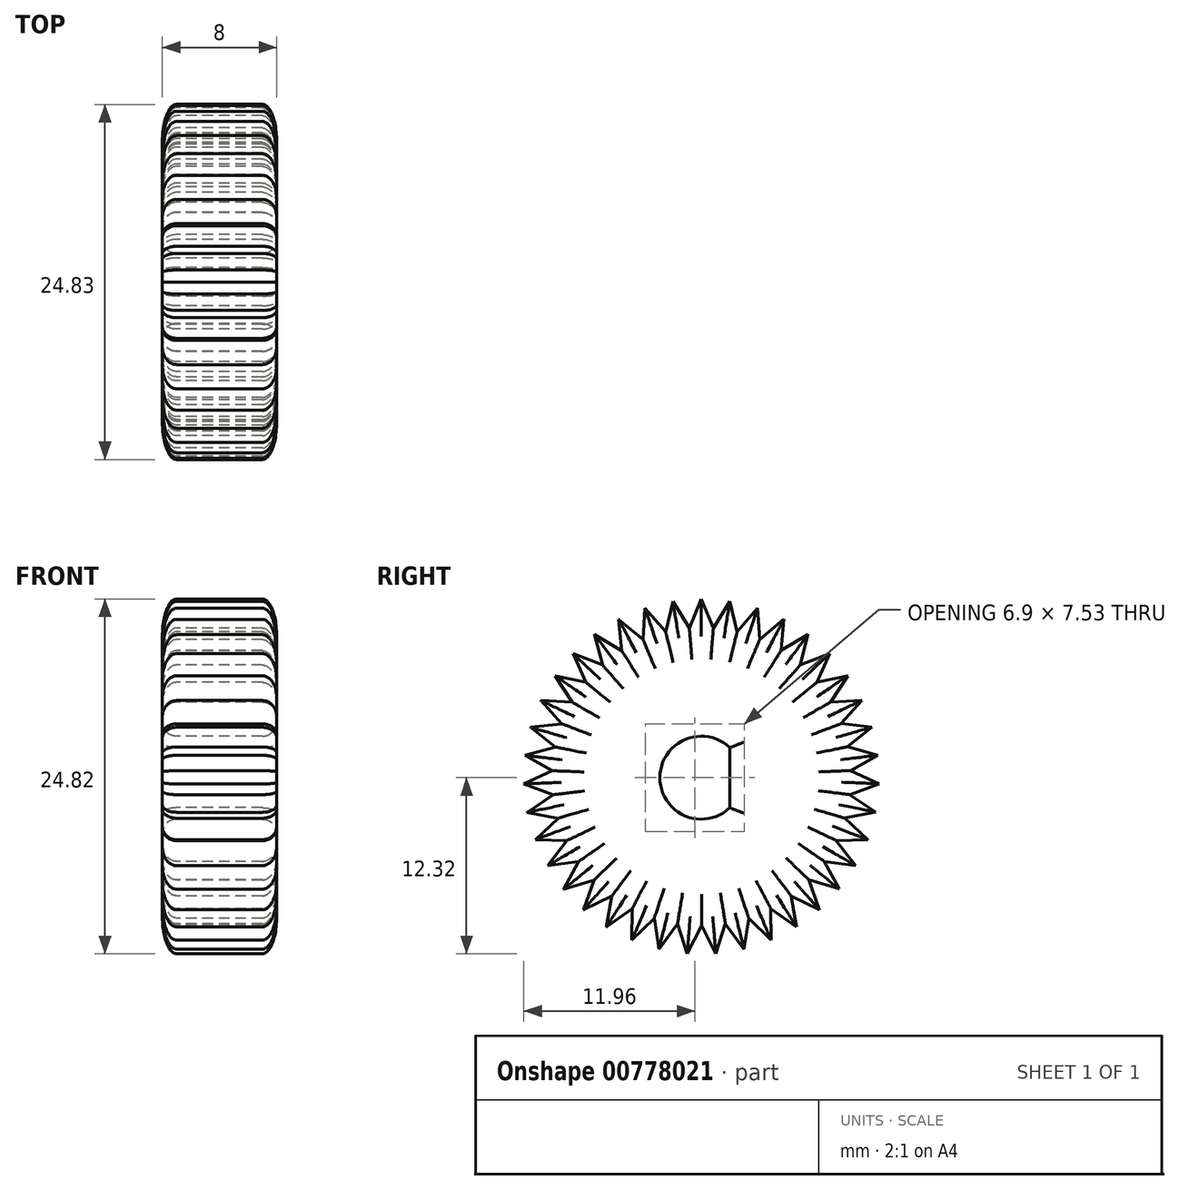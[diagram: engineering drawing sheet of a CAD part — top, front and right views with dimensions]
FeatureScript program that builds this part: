
annotation { "Feature Type Name" : "Feature", "Feature Type Description" : "" }
export const myFeature = defineFeature(function(context is Context, id is Id, definition is map)
    precondition{}
    {
        {
            var Q0;
            Q0=qCreatedBy(makeId("Right.planeOp"),FACE);
            var sketch = newSketch(context, id + "F0", { "sketchPlane" : qUnion([Q0])});
            skCircle(sketch, "E0", {"center": v(0, 0) * mm, "radius": 10.5 * mm, "construction": true});
            skCircle(sketch, "E1", {"center": v(0, 0) * mm, "radius": 2.9 * mm});
            skLineSegment(sketch, "E2", {"start": v(0, 0) * mm, "end": v(0, 12.5) * mm, "construction": true});
            skLineSegment(sketch, "E3", {"start": v(0, 12.5) * mm, "end": v(0.84, 10.47) * mm});
            skCircle(sketch, "E4", {"center": v(0, 0) * mm, "radius": 12.5 * mm, "construction": true});
            skLineSegment(sketch, "E5", {"start": v(0.84, 10.47) * mm, "end": v(2, 12.34) * mm});
            skLineSegment(sketch, "E6", {"start": v(2, 12.34) * mm, "end": v(0, 0) * mm, "construction": true});
            skLineSegment(sketch, "E7.1.0", {"start": v(-2, 12.34) * mm, "end": v(-0.84, 10.47) * mm});
            skLineSegment(sketch, "E7.1.1", {"start": v(-0.84, 10.47) * mm, "end": v(0, 12.5) * mm});
            skLineSegment(sketch, "E7.2.0", {"start": v(-3.94, 11.86) * mm, "end": v(-2.5, 10.2) * mm});
            skLineSegment(sketch, "E7.2.1", {"start": v(-2.5, 10.2) * mm, "end": v(-2, 12.34) * mm});
            skLineSegment(sketch, "E7.3.0", {"start": v(-5.77, 11.07) * mm, "end": v(-4.09, 9.66) * mm});
            skLineSegment(sketch, "E7.3.1", {"start": v(-4.09, 9.66) * mm, "end": v(-3.94, 11.86) * mm});
            skLineSegment(sketch, "E7.4.0", {"start": v(-7.46, 10) * mm, "end": v(-5.57, 8.88) * mm});
            skLineSegment(sketch, "E7.4.1", {"start": v(-5.57, 8.88) * mm, "end": v(-5.77, 11.07) * mm});
            skLineSegment(sketch, "E7.5.0", {"start": v(-8.96, 8.68) * mm, "end": v(-6.91, 7.87) * mm});
            skLineSegment(sketch, "E7.5.1", {"start": v(-6.91, 7.87) * mm, "end": v(-7.46, 10) * mm});
            skLineSegment(sketch, "E7.6.0", {"start": v(-10.23, 7.13) * mm, "end": v(-8.07, 6.66) * mm});
            skLineSegment(sketch, "E7.6.1", {"start": v(-8.07, 6.66) * mm, "end": v(-8.96, 8.68) * mm});
            skLineSegment(sketch, "E7.7.0", {"start": v(-11.22, 5.4) * mm, "end": v(-9.03, 5.28) * mm});
            skLineSegment(sketch, "E7.7.1", {"start": v(-9.03, 5.28) * mm, "end": v(-10.23, 7.13) * mm});
            skLineSegment(sketch, "E7.8.0", {"start": v(-11.93, 3.52) * mm, "end": v(-9.75, 3.77) * mm});
            skLineSegment(sketch, "E7.8.1", {"start": v(-9.75, 3.77) * mm, "end": v(-11.22, 5.4) * mm});
            skLineSegment(sketch, "E7.9.0", {"start": v(-12.33, 1.56) * mm, "end": v(-10.21, 2.15) * mm});
            skLineSegment(sketch, "E7.9.1", {"start": v(-10.21, 2.15) * mm, "end": v(-11.93, 3.52) * mm});
            skLineSegment(sketch, "E7.10.0", {"start": v(-12.41, -0.43) * mm, "end": v(-10.41, 0.49) * mm});
            skLineSegment(sketch, "E7.10.1", {"start": v(-10.41, 0.49) * mm, "end": v(-12.33, 1.56) * mm});
            skLineSegment(sketch, "E7.11.0", {"start": v(-12.17, -2.42) * mm, "end": v(-10.34, -1.19) * mm});
            skLineSegment(sketch, "E7.11.1", {"start": v(-10.34, -1.19) * mm, "end": v(-12.41, -0.43) * mm});
            skLineSegment(sketch, "E7.12.0", {"start": v(-11.61, -4.34) * mm, "end": v(-10, -2.83) * mm});
            skLineSegment(sketch, "E7.12.1", {"start": v(-10, -2.83) * mm, "end": v(-12.17, -2.42) * mm});
            skLineSegment(sketch, "E7.13.0", {"start": v(-10.75, -6.15) * mm, "end": v(-9.41, -4.4) * mm});
            skLineSegment(sketch, "E7.13.1", {"start": v(-9.41, -4.4) * mm, "end": v(-11.61, -4.34) * mm});
            skLineSegment(sketch, "E7.14.0", {"start": v(-9.62, -7.8) * mm, "end": v(-8.57, -5.85) * mm});
            skLineSegment(sketch, "E7.14.1", {"start": v(-8.57, -5.85) * mm, "end": v(-10.75, -6.15) * mm});
            skLineSegment(sketch, "E7.15.0", {"start": v(-8.23, -9.23) * mm, "end": v(-7.51, -7.15) * mm});
            skLineSegment(sketch, "E7.15.1", {"start": v(-7.51, -7.15) * mm, "end": v(-9.62, -7.8) * mm});
            skLineSegment(sketch, "E7.16.0", {"start": v(-6.63, -10.43) * mm, "end": v(-6.25, -8.27) * mm});
            skLineSegment(sketch, "E7.16.1", {"start": v(-6.25, -8.27) * mm, "end": v(-8.23, -9.23) * mm});
            skLineSegment(sketch, "E7.17.0", {"start": v(-4.86, -11.36) * mm, "end": v(-4.84, -9.16) * mm});
            skLineSegment(sketch, "E7.17.1", {"start": v(-4.84, -9.16) * mm, "end": v(-6.63, -10.43) * mm});
            skLineSegment(sketch, "E7.18.0", {"start": v(-2.96, -12) * mm, "end": v(-3.3, -9.82) * mm});
            skLineSegment(sketch, "E7.18.1", {"start": v(-3.3, -9.82) * mm, "end": v(-4.86, -11.36) * mm});
            skLineSegment(sketch, "E7.19.0", {"start": v(-0.99, -12.32) * mm, "end": v(-1.66, -10.22) * mm});
            skLineSegment(sketch, "E7.19.1", {"start": v(-1.66, -10.22) * mm, "end": v(-2.96, -12) * mm});
            skLineSegment(sketch, "E7.20.0", {"start": v(1.01, -12.31) * mm, "end": v(0.01, -10.35) * mm});
            skLineSegment(sketch, "E7.20.1", {"start": v(0.01, -10.35) * mm, "end": v(-0.99, -12.32) * mm});
            skLineSegment(sketch, "E7.21.0", {"start": v(2.99, -12) * mm, "end": v(1.68, -10.22) * mm});
            skLineSegment(sketch, "E7.21.1", {"start": v(1.68, -10.22) * mm, "end": v(1.01, -12.31) * mm});
            skLineSegment(sketch, "E7.22.0", {"start": v(4.88, -11.36) * mm, "end": v(3.31, -9.82) * mm});
            skLineSegment(sketch, "E7.22.1", {"start": v(3.31, -9.82) * mm, "end": v(2.99, -12) * mm});
            skLineSegment(sketch, "E7.23.0", {"start": v(6.65, -10.43) * mm, "end": v(4.86, -9.16) * mm});
            skLineSegment(sketch, "E7.23.1", {"start": v(4.86, -9.16) * mm, "end": v(4.88, -11.36) * mm});
            skLineSegment(sketch, "E7.24.0", {"start": v(8.25, -9.23) * mm, "end": v(6.27, -8.26) * mm});
            skLineSegment(sketch, "E7.24.1", {"start": v(6.27, -8.26) * mm, "end": v(6.65, -10.43) * mm});
            skLineSegment(sketch, "E7.25.0", {"start": v(9.64, -7.78) * mm, "end": v(7.53, -7.15) * mm});
            skLineSegment(sketch, "E7.25.1", {"start": v(7.53, -7.15) * mm, "end": v(8.25, -9.23) * mm});
            skLineSegment(sketch, "E7.26.0", {"start": v(10.77, -6.14) * mm, "end": v(8.6, -5.85) * mm});
            skLineSegment(sketch, "E7.26.1", {"start": v(8.6, -5.85) * mm, "end": v(9.64, -7.78) * mm});
            skLineSegment(sketch, "E7.27.0", {"start": v(11.63, -4.33) * mm, "end": v(9.43, -4.4) * mm});
            skLineSegment(sketch, "E7.27.1", {"start": v(9.43, -4.4) * mm, "end": v(10.77, -6.14) * mm});
            skLineSegment(sketch, "E7.28.0", {"start": v(12.18, -2.4) * mm, "end": v(10.02, -2.82) * mm});
            skLineSegment(sketch, "E7.28.1", {"start": v(10.02, -2.82) * mm, "end": v(11.63, -4.33) * mm});
            skLineSegment(sketch, "E7.29.0", {"start": v(12.42, -0.42) * mm, "end": v(10.36, -1.18) * mm});
            skLineSegment(sketch, "E7.29.1", {"start": v(10.36, -1.18) * mm, "end": v(12.18, -2.4) * mm});
            skLineSegment(sketch, "E7.30.0", {"start": v(12.34, 1.58) * mm, "end": v(10.42, 0.5) * mm});
            skLineSegment(sketch, "E7.30.1", {"start": v(10.42, 0.5) * mm, "end": v(12.42, -0.42) * mm});
            skLineSegment(sketch, "E7.31.0", {"start": v(11.94, 3.54) * mm, "end": v(10.22, 2.16) * mm});
            skLineSegment(sketch, "E7.31.1", {"start": v(10.22, 2.16) * mm, "end": v(12.34, 1.58) * mm});
            skLineSegment(sketch, "E7.32.0", {"start": v(11.23, 5.4) * mm, "end": v(9.75, 3.77) * mm});
            skLineSegment(sketch, "E7.32.1", {"start": v(9.75, 3.77) * mm, "end": v(11.94, 3.54) * mm});
            skLineSegment(sketch, "E7.33.0", {"start": v(10.23, 7.14) * mm, "end": v(9.03, 5.3) * mm});
            skLineSegment(sketch, "E7.33.1", {"start": v(9.03, 5.3) * mm, "end": v(11.23, 5.4) * mm});
            skLineSegment(sketch, "E7.34.0", {"start": v(8.96, 8.69) * mm, "end": v(8.08, 6.67) * mm});
            skLineSegment(sketch, "E7.34.1", {"start": v(8.08, 6.67) * mm, "end": v(10.23, 7.14) * mm});
            skLineSegment(sketch, "E7.35.0", {"start": v(7.47, 10.01) * mm, "end": v(6.92, 7.88) * mm});
            skLineSegment(sketch, "E7.35.1", {"start": v(6.92, 7.88) * mm, "end": v(8.96, 8.69) * mm});
            skLineSegment(sketch, "E7.36.0", {"start": v(5.78, 11.08) * mm, "end": v(5.57, 8.89) * mm});
            skLineSegment(sketch, "E7.36.1", {"start": v(5.57, 8.89) * mm, "end": v(7.47, 10.01) * mm});
            skLineSegment(sketch, "E7.37.0", {"start": v(3.94, 11.86) * mm, "end": v(4.09, 9.67) * mm});
            skLineSegment(sketch, "E7.37.1", {"start": v(4.09, 9.67) * mm, "end": v(5.78, 11.08) * mm});
            skLineSegment(sketch, "E7.38.0", {"start": v(2, 12.34) * mm, "end": v(2.5, 10.2) * mm});
            skLineSegment(sketch, "E7.38.1", {"start": v(2.5, 10.2) * mm, "end": v(3.94, 11.86) * mm});
            skPoint(sketch, "E7.center", {"position": v(0, 0.07) * mm});
            skSolve(sketch);
        }
        {
            var Q0;
            Q0=makeQuery(id+"F0.imprint","IMPRINT",FACE,{"disambiguationData":[TD([[makeQuery(id+"F0.imprint","IMPRINT",EDGE,{"derivedFrom":sQuery(id+"F0.wireOp",EDGE,"E1")}),-1.0]])]});
            extrude(context, id + "F1", {"entities" : qUnion([Q0]), "depth" : 8 * mm, "offsetDistance" : 25.4 * mm});
        }
        {
            var Q0;
            Q0=qCreatedBy(makeId("Right.planeOp"),FACE);
            var sketch = newSketch(context, id + "F2", { "sketchPlane" : qUnion([Q0])});
            skLineSegment(sketch, "E8", {"start": v(2, 2.1) * mm, "end": v(2, -2.1) * mm});
            skArc(sketch, "E9", {"start": v(2, -2.1) * mm, "mid": v(2.9, 0) * mm, "end": v(2, 2.1) * mm});
            skSolve(sketch);
        }
        {
            var Q0;
            Q0 = qSketchRegion(id + "F2", true);
            extrude(context, id + "F3", {"entities" : qUnion([Q0]), "operationType" : NewBodyOperationType.ADD, "depth" : 8 * mm, "offsetDistance" : 25.4 * mm});
        }
        {
            var Q0;
            Q0=makeQuery(id+"F3.boolean.opBoolean","MERGE",FACE,{"derivedFrom":[makeQuery(id+"F1.opExtrude","CAP_FACE",FACE,{"disambiguationData":[OSD([sQuery(id+"F0.wireOp",EDGE,"E1"),sQuery(id+"F0.wireOp",EDGE,"E3"),sQuery(id+"F0.wireOp",EDGE,"E5"),sQuery(id+"F0.wireOp",EDGE,"E7.1.0"),sQuery(id+"F0.wireOp",EDGE,"E7.1.1"),sQuery(id+"F0.wireOp",EDGE,"E7.2.0"),sQuery(id+"F0.wireOp",EDGE,"E7.2.1"),sQuery(id+"F0.wireOp",EDGE,"E7.3.0"),sQuery(id+"F0.wireOp",EDGE,"E7.3.1"),sQuery(id+"F0.wireOp",EDGE,"E7.4.0"),sQuery(id+"F0.wireOp",EDGE,"E7.4.1"),sQuery(id+"F0.wireOp",EDGE,"E7.5.0"),sQuery(id+"F0.wireOp",EDGE,"E7.5.1"),sQuery(id+"F0.wireOp",EDGE,"E7.6.0"),sQuery(id+"F0.wireOp",EDGE,"E7.6.1"),sQuery(id+"F0.wireOp",EDGE,"E7.7.0"),sQuery(id+"F0.wireOp",EDGE,"E7.7.1"),sQuery(id+"F0.wireOp",EDGE,"E7.8.0"),sQuery(id+"F0.wireOp",EDGE,"E7.8.1"),sQuery(id+"F0.wireOp",EDGE,"E7.9.0"),sQuery(id+"F0.wireOp",EDGE,"E7.9.1"),sQuery(id+"F0.wireOp",EDGE,"E7.10.0"),sQuery(id+"F0.wireOp",EDGE,"E7.10.1"),sQuery(id+"F0.wireOp",EDGE,"E7.11.0"),sQuery(id+"F0.wireOp",EDGE,"E7.11.1"),sQuery(id+"F0.wireOp",EDGE,"E7.12.0"),sQuery(id+"F0.wireOp",EDGE,"E7.12.1"),sQuery(id+"F0.wireOp",EDGE,"E7.13.0"),sQuery(id+"F0.wireOp",EDGE,"E7.13.1"),sQuery(id+"F0.wireOp",EDGE,"E7.14.0"),sQuery(id+"F0.wireOp",EDGE,"E7.14.1"),sQuery(id+"F0.wireOp",EDGE,"E7.15.0"),sQuery(id+"F0.wireOp",EDGE,"E7.15.1"),sQuery(id+"F0.wireOp",EDGE,"E7.16.0"),sQuery(id+"F0.wireOp",EDGE,"E7.16.1"),sQuery(id+"F0.wireOp",EDGE,"E7.17.0"),sQuery(id+"F0.wireOp",EDGE,"E7.17.1"),sQuery(id+"F0.wireOp",EDGE,"E7.18.0"),sQuery(id+"F0.wireOp",EDGE,"E7.18.1"),sQuery(id+"F0.wireOp",EDGE,"E7.19.0"),sQuery(id+"F0.wireOp",EDGE,"E7.19.1"),sQuery(id+"F0.wireOp",EDGE,"E7.20.0"),sQuery(id+"F0.wireOp",EDGE,"E7.20.1"),sQuery(id+"F0.wireOp",EDGE,"E7.21.0"),sQuery(id+"F0.wireOp",EDGE,"E7.21.1"),sQuery(id+"F0.wireOp",EDGE,"E7.22.0"),sQuery(id+"F0.wireOp",EDGE,"E7.22.1"),sQuery(id+"F0.wireOp",EDGE,"E7.23.0"),sQuery(id+"F0.wireOp",EDGE,"E7.23.1"),sQuery(id+"F0.wireOp",EDGE,"E7.24.0"),sQuery(id+"F0.wireOp",EDGE,"E7.24.1"),sQuery(id+"F0.wireOp",EDGE,"E7.25.0"),sQuery(id+"F0.wireOp",EDGE,"E7.25.1"),sQuery(id+"F0.wireOp",EDGE,"E7.26.0"),sQuery(id+"F0.wireOp",EDGE,"E7.26.1"),sQuery(id+"F0.wireOp",EDGE,"E7.27.0"),sQuery(id+"F0.wireOp",EDGE,"E7.27.1"),sQuery(id+"F0.wireOp",EDGE,"E7.28.0"),sQuery(id+"F0.wireOp",EDGE,"E7.28.1"),sQuery(id+"F0.wireOp",EDGE,"E7.29.0"),sQuery(id+"F0.wireOp",EDGE,"E7.29.1"),sQuery(id+"F0.wireOp",EDGE,"E7.30.0"),sQuery(id+"F0.wireOp",EDGE,"E7.30.1"),sQuery(id+"F0.wireOp",EDGE,"E7.31.0"),sQuery(id+"F0.wireOp",EDGE,"E7.31.1"),sQuery(id+"F0.wireOp",EDGE,"E7.32.0"),sQuery(id+"F0.wireOp",EDGE,"E7.32.1"),sQuery(id+"F0.wireOp",EDGE,"E7.33.0"),sQuery(id+"F0.wireOp",EDGE,"E7.33.1"),sQuery(id+"F0.wireOp",EDGE,"E7.34.0"),sQuery(id+"F0.wireOp",EDGE,"E7.34.1"),sQuery(id+"F0.wireOp",EDGE,"E7.35.0"),sQuery(id+"F0.wireOp",EDGE,"E7.35.1"),sQuery(id+"F0.wireOp",EDGE,"E7.36.0"),sQuery(id+"F0.wireOp",EDGE,"E7.36.1"),sQuery(id+"F0.wireOp",EDGE,"E7.37.0"),sQuery(id+"F0.wireOp",EDGE,"E7.37.1"),sQuery(id+"F0.wireOp",EDGE,"E7.38.0"),sQuery(id+"F0.wireOp",EDGE,"E7.38.1")])],"isStart":false}),makeQuery(id+"F3.opExtrude","CAP_FACE",FACE,{"disambiguationData":[OSD([sQuery(id+"F2.wireOp",EDGE,"E8"),sQuery(id+"F2.wireOp",EDGE,"E9")])],"isStart":false})]});
            fillet(context, id + "F4", {"entities" : qUnion([Q0]), "radius" : 1 * mm, "tangentPropagation" : true, "allowEdgeOverflow" : false});
        }
        {
            var Q0;
            Q0=makeQuery(id+"F3.boolean.opBoolean","MERGE",FACE,{"derivedFrom":[makeQuery(id+"F1.opExtrude","CAP_FACE",FACE,{"disambiguationData":[OSD([sQuery(id+"F0.wireOp",EDGE,"E1"),sQuery(id+"F0.wireOp",EDGE,"E3"),sQuery(id+"F0.wireOp",EDGE,"E5"),sQuery(id+"F0.wireOp",EDGE,"E7.1.0"),sQuery(id+"F0.wireOp",EDGE,"E7.1.1"),sQuery(id+"F0.wireOp",EDGE,"E7.2.0"),sQuery(id+"F0.wireOp",EDGE,"E7.2.1"),sQuery(id+"F0.wireOp",EDGE,"E7.3.0"),sQuery(id+"F0.wireOp",EDGE,"E7.3.1"),sQuery(id+"F0.wireOp",EDGE,"E7.4.0"),sQuery(id+"F0.wireOp",EDGE,"E7.4.1"),sQuery(id+"F0.wireOp",EDGE,"E7.5.0"),sQuery(id+"F0.wireOp",EDGE,"E7.5.1"),sQuery(id+"F0.wireOp",EDGE,"E7.6.0"),sQuery(id+"F0.wireOp",EDGE,"E7.6.1"),sQuery(id+"F0.wireOp",EDGE,"E7.7.0"),sQuery(id+"F0.wireOp",EDGE,"E7.7.1"),sQuery(id+"F0.wireOp",EDGE,"E7.8.0"),sQuery(id+"F0.wireOp",EDGE,"E7.8.1"),sQuery(id+"F0.wireOp",EDGE,"E7.9.0"),sQuery(id+"F0.wireOp",EDGE,"E7.9.1"),sQuery(id+"F0.wireOp",EDGE,"E7.10.0"),sQuery(id+"F0.wireOp",EDGE,"E7.10.1"),sQuery(id+"F0.wireOp",EDGE,"E7.11.0"),sQuery(id+"F0.wireOp",EDGE,"E7.11.1"),sQuery(id+"F0.wireOp",EDGE,"E7.12.0"),sQuery(id+"F0.wireOp",EDGE,"E7.12.1"),sQuery(id+"F0.wireOp",EDGE,"E7.13.0"),sQuery(id+"F0.wireOp",EDGE,"E7.13.1"),sQuery(id+"F0.wireOp",EDGE,"E7.14.0"),sQuery(id+"F0.wireOp",EDGE,"E7.14.1"),sQuery(id+"F0.wireOp",EDGE,"E7.15.0"),sQuery(id+"F0.wireOp",EDGE,"E7.15.1"),sQuery(id+"F0.wireOp",EDGE,"E7.16.0"),sQuery(id+"F0.wireOp",EDGE,"E7.16.1"),sQuery(id+"F0.wireOp",EDGE,"E7.17.0"),sQuery(id+"F0.wireOp",EDGE,"E7.17.1"),sQuery(id+"F0.wireOp",EDGE,"E7.18.0"),sQuery(id+"F0.wireOp",EDGE,"E7.18.1"),sQuery(id+"F0.wireOp",EDGE,"E7.19.0"),sQuery(id+"F0.wireOp",EDGE,"E7.19.1"),sQuery(id+"F0.wireOp",EDGE,"E7.20.0"),sQuery(id+"F0.wireOp",EDGE,"E7.20.1"),sQuery(id+"F0.wireOp",EDGE,"E7.21.0"),sQuery(id+"F0.wireOp",EDGE,"E7.21.1"),sQuery(id+"F0.wireOp",EDGE,"E7.22.0"),sQuery(id+"F0.wireOp",EDGE,"E7.22.1"),sQuery(id+"F0.wireOp",EDGE,"E7.23.0"),sQuery(id+"F0.wireOp",EDGE,"E7.23.1"),sQuery(id+"F0.wireOp",EDGE,"E7.24.0"),sQuery(id+"F0.wireOp",EDGE,"E7.24.1"),sQuery(id+"F0.wireOp",EDGE,"E7.25.0"),sQuery(id+"F0.wireOp",EDGE,"E7.25.1"),sQuery(id+"F0.wireOp",EDGE,"E7.26.0"),sQuery(id+"F0.wireOp",EDGE,"E7.26.1"),sQuery(id+"F0.wireOp",EDGE,"E7.27.0"),sQuery(id+"F0.wireOp",EDGE,"E7.27.1"),sQuery(id+"F0.wireOp",EDGE,"E7.28.0"),sQuery(id+"F0.wireOp",EDGE,"E7.28.1"),sQuery(id+"F0.wireOp",EDGE,"E7.29.0"),sQuery(id+"F0.wireOp",EDGE,"E7.29.1"),sQuery(id+"F0.wireOp",EDGE,"E7.30.0"),sQuery(id+"F0.wireOp",EDGE,"E7.30.1"),sQuery(id+"F0.wireOp",EDGE,"E7.31.0"),sQuery(id+"F0.wireOp",EDGE,"E7.31.1"),sQuery(id+"F0.wireOp",EDGE,"E7.32.0"),sQuery(id+"F0.wireOp",EDGE,"E7.32.1"),sQuery(id+"F0.wireOp",EDGE,"E7.33.0"),sQuery(id+"F0.wireOp",EDGE,"E7.33.1"),sQuery(id+"F0.wireOp",EDGE,"E7.34.0"),sQuery(id+"F0.wireOp",EDGE,"E7.34.1"),sQuery(id+"F0.wireOp",EDGE,"E7.35.0"),sQuery(id+"F0.wireOp",EDGE,"E7.35.1"),sQuery(id+"F0.wireOp",EDGE,"E7.36.0"),sQuery(id+"F0.wireOp",EDGE,"E7.36.1"),sQuery(id+"F0.wireOp",EDGE,"E7.37.0"),sQuery(id+"F0.wireOp",EDGE,"E7.37.1"),sQuery(id+"F0.wireOp",EDGE,"E7.38.0"),sQuery(id+"F0.wireOp",EDGE,"E7.38.1")])],"isStart":true}),makeQuery(id+"F3.opExtrude","CAP_FACE",FACE,{"disambiguationData":[OSD([sQuery(id+"F2.wireOp",EDGE,"E8"),sQuery(id+"F2.wireOp",EDGE,"E9")])],"isStart":true})]});
            fillet(context, id + "F5", {"entities" : qUnion([Q0]), "radius" : 1 * mm, "tangentPropagation" : true, "allowEdgeOverflow" : false});
        }
    });
